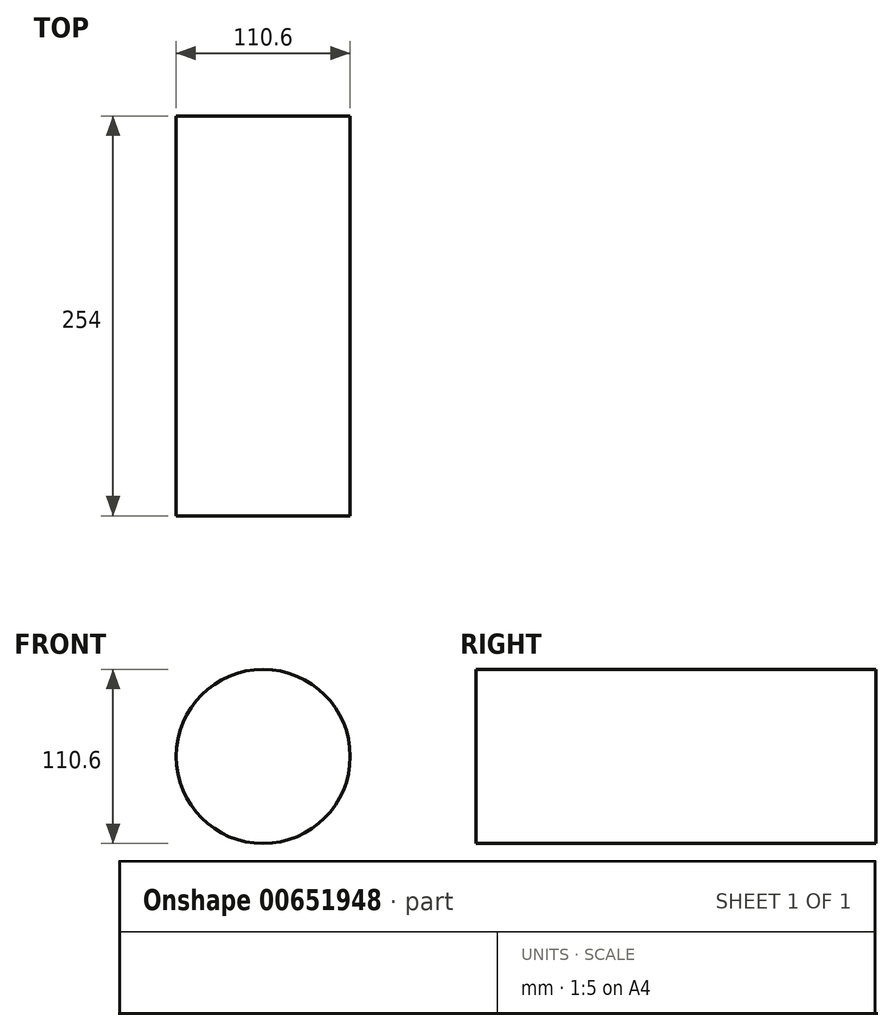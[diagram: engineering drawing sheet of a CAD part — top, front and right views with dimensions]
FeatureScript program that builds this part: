
annotation { "Feature Type Name" : "Feature", "Feature Type Description" : "" }
export const myFeature = defineFeature(function(context is Context, id is Id, definition is map)
    precondition{}
    {
        {
            var Q0;
            Q0=qCreatedBy(makeId("Front.planeOp"),FACE);
            var sketch = newSketch(context, id + "F0", { "sketchPlane" : qUnion([Q0])});
            skCircle(sketch, "E0", {"center": v(0, 0) * mm, "radius": 55.3 * mm});
            skSolve(sketch);
        }
        {
            var Q0;
            Q0=makeQuery(id+"F0.imprint","IMPRINT",FACE,{"disambiguationData":[TD([[makeQuery(id+"F0.imprint","IMPRINT",EDGE,{"derivedFrom":sQuery(id+"F0.wireOp",EDGE,"E0")}),1.0]])]});
            extrude(context, id + "F1", {"entities" : qUnion([Q0]), "depth" : 254 * mm, "offsetDistance" : 25.4 * mm});
        }
    });
